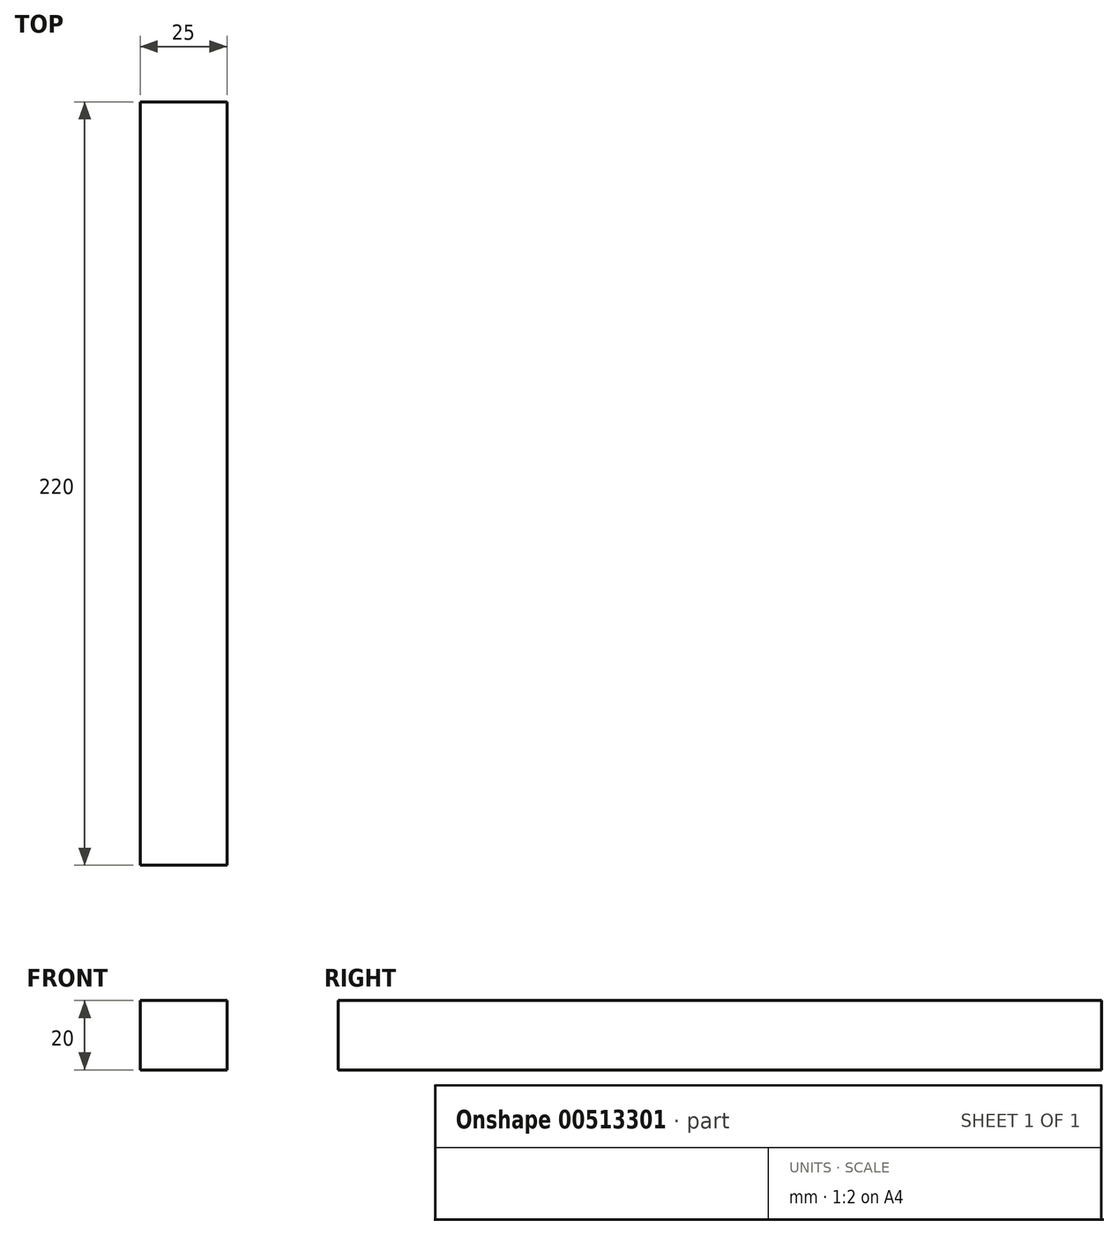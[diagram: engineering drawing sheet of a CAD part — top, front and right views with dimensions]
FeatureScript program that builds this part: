
annotation { "Feature Type Name" : "Feature", "Feature Type Description" : "" }
export const myFeature = defineFeature(function(context is Context, id is Id, definition is map)
    precondition{}
    {
        {
            var Q0;
            Q0=qCreatedBy(makeId("Front.planeOp"),FACE);
            var sketch = newSketch(context, id + "F0", { "sketchPlane" : qUnion([Q0])});
            skLineSegment(sketch, "E0.bottom", {"start": v(12.5, 10) * mm, "end": v(-12.5, 10) * mm});
            skLineSegment(sketch, "E0.top", {"start": v(12.5, -10) * mm, "end": v(-12.5, -10) * mm});
            skLineSegment(sketch, "E0.left", {"start": v(12.5, 10) * mm, "end": v(12.5, -10) * mm});
            skLineSegment(sketch, "E0.right", {"start": v(-12.5, 10) * mm, "end": v(-12.5, -10) * mm});
            skPoint(sketch, "E0.middle", {"position": v(0, 0) * mm});
            skSolve(sketch);
        }
        {
            var Q0;
            Q0 = qSketchRegion(id + "F0", true);
            extrude(context, id + "F1", {"entities" : qUnion([Q0]), "depth" : 220 * mm, "offsetDistance" : 25 * mm});
        }
    });
